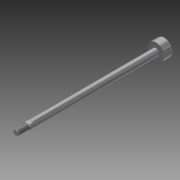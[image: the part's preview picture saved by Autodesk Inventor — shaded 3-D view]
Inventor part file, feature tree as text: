
AUTODESK INVENTOR PART (.ipt)
format: ipt  version: 2016 SP1 (Build 200210100, 210)  size: 107,520 bytes
history: native  units: in
note: dims shown in document units (in); Inventor stores cm internally (conversion verified against a paired STEP export)
features: other x7, sketch x3, extrude x2, revolve x1, thread x1
ambient origin geometry x8: Origin, YZ Plane, XZ Plane, XY Plane, X Axis, Y Axis, Z Axis, Center Point
bodies: Solid1 (feature_tree)
feature tree (14):
  revolve  "Revolution1"  [1 undecoded]
  thread  "Thread1"  [1 undecoded]
  extrude  "Extrusion1"  TaperAngle=0.0deg  [1 undecoded]
  extrude  "Extrusion2"  [1 undecoded]
  other  "conn_XY"
  other  "conn_YZ"
  other  "conn_ZX"
  other  "conn_X"
  other  "conn_Y"
  other  "conn_Z"
  other  "conn_Center"
  sketch  "Sketch_1"  dims[d0=360.0deg d1=0.4787in d2=0.0in d3=0.63in d4=0.0in]
  sketch  "Sketch_2"  dims[d5=0.63in d6=0.0in d7=0.0in]
  sketch  "Sketch_3"
note: 4 required parameter values undecoded (feature->parameter linkage not recoverable at this tier; creation-order binding heuristic only, values carry confidence <= 0.55)